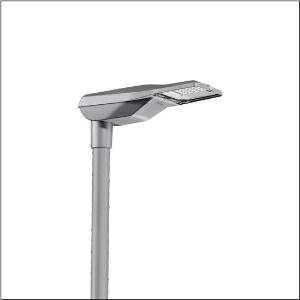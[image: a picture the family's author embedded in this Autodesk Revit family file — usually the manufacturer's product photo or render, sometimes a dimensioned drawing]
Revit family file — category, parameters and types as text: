
# Revit family: streetlight_sl_21_iq_micro___stw1_0a_5xe1e31d08db_99ec
name_source: partatom
category: Lighting Fixtures
units: mm (PartAtom-declared; Revit-internal decimal feet)

## family parameters
Cut with Voids When Loaded = No
Host = Face
Light Source = No
Part Type = Normal
Room Calculation Point = No
Round Connector Dimension = Use Diameter
Shared = No

## types (1)
- --- (1 x LED, 4810 lm, 36.4 W, 3000K)
    Apparent Load = 36 VA
    CIE Flux Codes = 38 75 98 100 100
    Color Rendering = 70
    Color Temperature = 3000K
    Default Elevation = 1800 mm
    Description = Streetlight SL 21 iQ micro, mast luminaire, primary light control with lens, of PMMA, primary optical cover: cover, of toughened safety glass, transparent, light distribution: STW1.0a, light emission: direct distribution, primary light characteristic: asymmetric, installation type: post-top, side-entry, LED, High Power LED, rated luminous flux: 4.810lm, luminous efficacy: 132lm/W, light colour: 730, colour temperature: 3000K, control gear: iQ-Comfort, control: Auto-Match, Temp-Guard, Lumen-Switch, Night-Set, Smart-Wire, Light-Fading, Desk-Remote (wireless, voltage-free reading and setting of iQ features in the workshop via application-optimized NFC function/RFID function), optimised constant luminous flux control (CLO 2.0), pre-setting: linear dimming characteristic, mains connection: 220..240V, AC, 50/60Hz, start of lifetime: 36W, end of service life: 38W, reduction: 16W, luminaire housing, of diecast aluminium, powder-coated, SITECO metallic grey (DB 702S), corrosivity category C5 high according to DIN EN ISO 12944, please order mast flange separately, inclination adjustable: 0°, 5°, 10°, 15°, sealing non-destructively replaceable, multi-level sealing system, length: 528mm, width: 235mm, height: 110mm, mast flange for spigot size: 42mm (side-entry): 5XC10008XM4, 60/48mm (side-entry/post-top): 5XC10108XM2, 76/60mm (side-entry/post-top): 5XC10108XM1, protection rating (complete): IP66, insulation class (complete): insulation class II (safety insulation), certification: CE, ENEC, ENEC+, VDE, impact resistance: IK10, permissible operating ambient temperature for outdoor applications: -40..+50°C, standard-compliant lighting for roads and squares, packaging unit: 1 piece

Light Distribution: STW1.0a
    Height = 110 mm
    Lamp = 1 x LED
    Lamp Light Flux = 4810 lm
    Lamp Power = 36.4 W
    Lamp count = 1
    Length = 528 mm
    Luminous efficacy = 132 lm/W
    Manufacturer = Siteco
    ModVariant = No
    Model = 5XE1E31D08DB
    Mounting Place = Pole
    Mounting Type = Pole top
    Number of Poles = 1
    OnlyDefault = Yes
    Power Factor = 1
    Product Name = Streetlight SL 21 iQ micro | STW1.0a
    Product group = mast luminaire | pylon top
    ProductGroupID = 6100
    Protection Class = Protection class II
    Protection Degree = IP 66
    RLX_Detail_Level = 1
    RLX_Emergency_Light_Flux = 0 lm
    RLX_Emergency_Type = 0
    RLX_Emergency_Type_DB = No
    RlxData = <blob elided: 99261 chars, md5=77352833>
    Socket = socket
    Standby Power = 0 W
    System Light Flux = 4810 lm
    System Power = 36 W
    Type Comments = factory setting: luminous flux: 100 % | dim-lin: 254 | 715 mA
    Type Image = l_1006881.jpg
    URL = http://relux.com
    VarID = @adj_156547
    Voltage = 0 V
    Weight = 0.00 kg
    Width = 235 mm

## geometry (parser evidence)
native form markers: Blend x4, Sweep x10
no freeform markers — native parametric forms only
